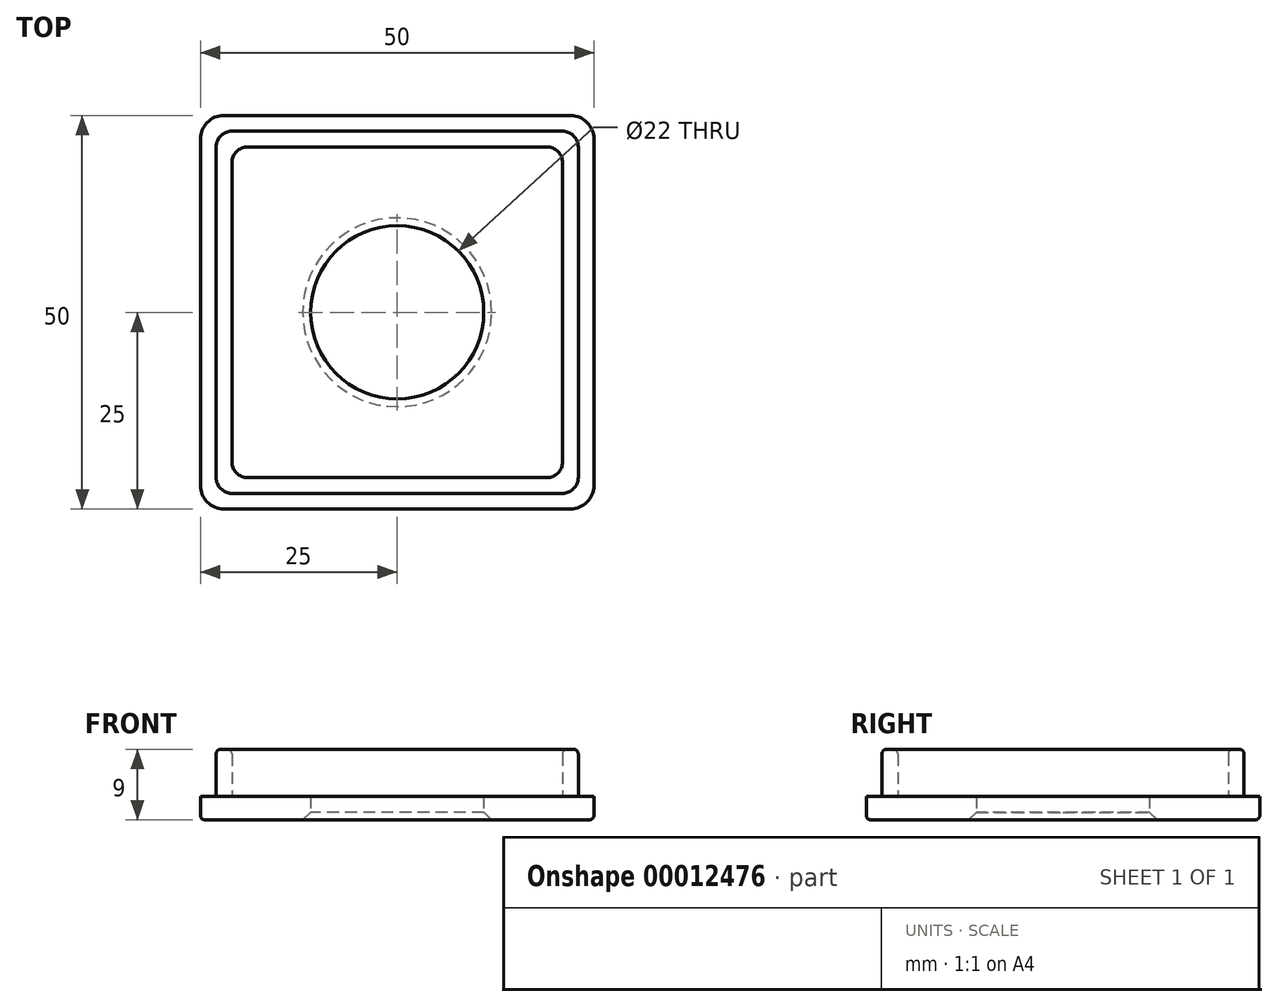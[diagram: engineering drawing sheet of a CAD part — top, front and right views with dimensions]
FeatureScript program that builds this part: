
annotation { "Feature Type Name" : "Feature", "Feature Type Description" : "" }
export const myFeature = defineFeature(function(context is Context, id is Id, definition is map)
    precondition{}
    {
        {
            var Q0;
            Q0=qCreatedBy(makeId("Top.planeOp"),FACE);
            var sketch = newSketch(context, id + "F0", { "sketchPlane" : qUnion([Q0])});
            skLineSegment(sketch, "E0.rect.bottom", {"start": v(-25, -25) * mm, "end": v(25, -25) * mm});
            skLineSegment(sketch, "E0.rect.top", {"start": v(-25, 25) * mm, "end": v(25, 25) * mm});
            skLineSegment(sketch, "E0.rect.left", {"start": v(-25, -25) * mm, "end": v(-25, 25) * mm});
            skLineSegment(sketch, "E0.rect.right", {"start": v(25, -25) * mm, "end": v(25, 25) * mm});
            skPoint(sketch, "E0.rect.middle", {"position": v(0, 0) * mm});
            skLineSegment(sketch, "E1.0", {"start": v(-23, 23) * mm, "end": v(23, 23) * mm});
            skLineSegment(sketch, "E1.1", {"start": v(-23, -23) * mm, "end": v(-23, 23) * mm});
            skLineSegment(sketch, "E1.2", {"start": v(-23, -23) * mm, "end": v(23, -23) * mm});
            skLineSegment(sketch, "E1.3", {"start": v(23, -23) * mm, "end": v(23, 23) * mm});
            skLineSegment(sketch, "E2.0", {"start": v(-21, -21) * mm, "end": v(21, -21) * mm});
            skLineSegment(sketch, "E2.1", {"start": v(-21, -21) * mm, "end": v(-21, 21) * mm});
            skLineSegment(sketch, "E2.2", {"start": v(-21, 21) * mm, "end": v(21, 21) * mm});
            skLineSegment(sketch, "E2.3", {"start": v(21, -21) * mm, "end": v(21, 21) * mm});
            skCircle(sketch, "E3", {"center": v(0, 0) * mm, "radius": 11 * mm});
            skSolve(sketch);
        }
        {
            var Q0;
            Q0 = qSketchRegion(id + "F0", true);
            extrude(context, id + "F1", {"entities" : qUnion([Q0]), "depth" : 3 * mm});
        }
        {
            var Q0;
            Q0=makeQuery(id+"F1.opExtrude","SWEPT_EDGE",EDGE,{"disambiguationData":[OSD([sQuery(id+"F0.wireOp",EDGE,"E0.rect.bottom"),sQuery(id+"F0.wireOp",EDGE,"E0.rect.left")])]});
            var Q1;
            Q1=makeQuery(id+"F1.opExtrude","SWEPT_EDGE",EDGE,{"disambiguationData":[OSD([sQuery(id+"F0.wireOp",EDGE,"E0.rect.bottom"),sQuery(id+"F0.wireOp",EDGE,"E0.rect.right")])]});
            var Q2;
            Q2=makeQuery(id+"F1.opExtrude","SWEPT_EDGE",EDGE,{"disambiguationData":[OSD([sQuery(id+"F0.wireOp",EDGE,"E0.rect.top"),sQuery(id+"F0.wireOp",EDGE,"E0.rect.left")])]});
            var Q3;
            Q3=makeQuery(id+"F1.opExtrude","SWEPT_EDGE",EDGE,{"disambiguationData":[OSD([sQuery(id+"F0.wireOp",EDGE,"E0.rect.top"),sQuery(id+"F0.wireOp",EDGE,"E0.rect.right")])]});
            fillet(context, id + "F2", {"entities" : qUnion([Q0, Q1, Q2, Q3]), "radius" : 3 * mm, "tangentPropagation" : true, "allowEdgeOverflow" : false});
        }
        {
            var Q0;
            Q0=makeQuery(id+"F0.imprint","IMPRINT",FACE,{"disambiguationData":[TD([[makeQuery(id+"F0.imprint","IMPRINT",EDGE,{"derivedFrom":sQuery(id+"F0.wireOp",EDGE,"E1.0")}),-1.0]])]});
            extrude(context, id + "F3", {"entities" : qUnion([Q0]), "operationType" : NewBodyOperationType.ADD, "depth" : 9 * mm});
        }
        {
            var Q0;
            Q0=makeQuery(id+"F3.opExtrude","SWEPT_EDGE",EDGE,{"disambiguationData":[OSD([sQuery(id+"F0.wireOp",EDGE,"E1.1"),sQuery(id+"F0.wireOp",EDGE,"E1.2")])]});
            var Q1;
            Q1=makeQuery(id+"F3.opExtrude","SWEPT_EDGE",EDGE,{"disambiguationData":[OSD([sQuery(id+"F0.wireOp",EDGE,"E1.0"),sQuery(id+"F0.wireOp",EDGE,"E1.1")])]});
            var Q2;
            Q2=makeQuery(id+"F3.opExtrude","SWEPT_EDGE",EDGE,{"disambiguationData":[OSD([sQuery(id+"F0.wireOp",EDGE,"E1.2"),sQuery(id+"F0.wireOp",EDGE,"E1.3")])]});
            var Q3;
            Q3=makeQuery(id+"F3.opExtrude","SWEPT_EDGE",EDGE,{"disambiguationData":[OSD([sQuery(id+"F0.wireOp",EDGE,"E1.0"),sQuery(id+"F0.wireOp",EDGE,"E1.3")])]});
            fillet(context, id + "F4", {"entities" : qUnion([Q0, Q1, Q2, Q3]), "radius" : 2 * mm, "tangentPropagation" : true, "allowEdgeOverflow" : false});
        }
        {
            var Q0;
            Q0=makeQuery(id+"F0.imprint","IMPRINT",FACE,{"disambiguationData":[TD([[makeQuery(id+"F0.imprint","IMPRINT",EDGE,{"derivedFrom":sQuery(id+"F0.wireOp",EDGE,"E2.0")}),1.0]])]});
            extrude(context, id + "F5", {"entities" : qUnion([Q0]), "operationType" : NewBodyOperationType.ADD, "depth" : 3 * mm});
        }
        {
            var Q0;
            Q0=makeQuery(id+"F3.opExtrude","SWEPT_EDGE",EDGE,{"disambiguationData":[OSD([sQuery(id+"F0.wireOp",EDGE,"E2.2"),sQuery(id+"F0.wireOp",EDGE,"E2.3")])]});
            var Q1;
            Q1=makeQuery(id+"F3.opExtrude","SWEPT_EDGE",EDGE,{"disambiguationData":[OSD([sQuery(id+"F0.wireOp",EDGE,"E2.0"),sQuery(id+"F0.wireOp",EDGE,"E2.3")])]});
            var Q2;
            Q2=makeQuery(id+"F3.opExtrude","SWEPT_EDGE",EDGE,{"disambiguationData":[OSD([sQuery(id+"F0.wireOp",EDGE,"E2.1"),sQuery(id+"F0.wireOp",EDGE,"E2.2")])]});
            var Q3;
            Q3=makeQuery(id+"F3.opExtrude","SWEPT_EDGE",EDGE,{"disambiguationData":[OSD([sQuery(id+"F0.wireOp",EDGE,"E2.0"),sQuery(id+"F0.wireOp",EDGE,"E2.1")])]});
            fillet(context, id + "F6", {"entities" : qUnion([Q0, Q1, Q2, Q3]), "radius" : 2 * mm, "tangentPropagation" : true, "allowEdgeOverflow" : false});
        }
        {
            var Q0;
            Q0=makeQuery(id+"F0.imprint","IMPRINT",FACE,{"disambiguationData":[TD([[makeQuery(id+"F0.imprint","IMPRINT",EDGE,{"derivedFrom":sQuery(id+"F0.wireOp",EDGE,"E3")}),1.0]])]});
            extrude(context, id + "F7", {"entities" : qUnion([Q0]), "operationType" : NewBodyOperationType.REMOVE, "depth" : 25 * mm, "hasSecondDirection" : true, "secondDirectionOppositeDirection" : true, "secondDirectionDepth" : 25 * mm});
        }
        {
            var Q0;
            Q0=makeQuery(id+"F1.opExtrude","CAP_EDGE",EDGE,{"disambiguationData":[OSD([sQuery(id+"F0.wireOp",EDGE,"E0.rect.top")])],"isStart":true});
            var Q1;
            Q1=makeQuery(id+"F3.opExtrude","CAP_EDGE",EDGE,{"disambiguationData":[OSD([sQuery(id+"F0.wireOp",EDGE,"E1.1")])],"isStart":false});
            var Q2;
            Q2=makeQuery(id+"F3.opExtrude","CAP_EDGE",EDGE,{"disambiguationData":[OSD([sQuery(id+"F0.wireOp",EDGE,"E2.1")])],"isStart":false});
            fillet(context, id + "F8", {"entities" : qUnion([Q0, Q1, Q2]), "radius" : 0.62 * mm, "tangentPropagation" : true, "allowEdgeOverflow" : false});
        }
        {
            var Q0;
            Q0=makeQuery(id+"F5.opExtrude","CAP_EDGE",EDGE,{"disambiguationData":[OSD([sQuery(id+"F0.wireOp",EDGE,"E3")])],"isStart":true});
            chamfer(context, id + "F9", {"entities" : qUnion([Q0]), "width" : 1 * mm, "tangentPropagation" : true});
        }
    });
